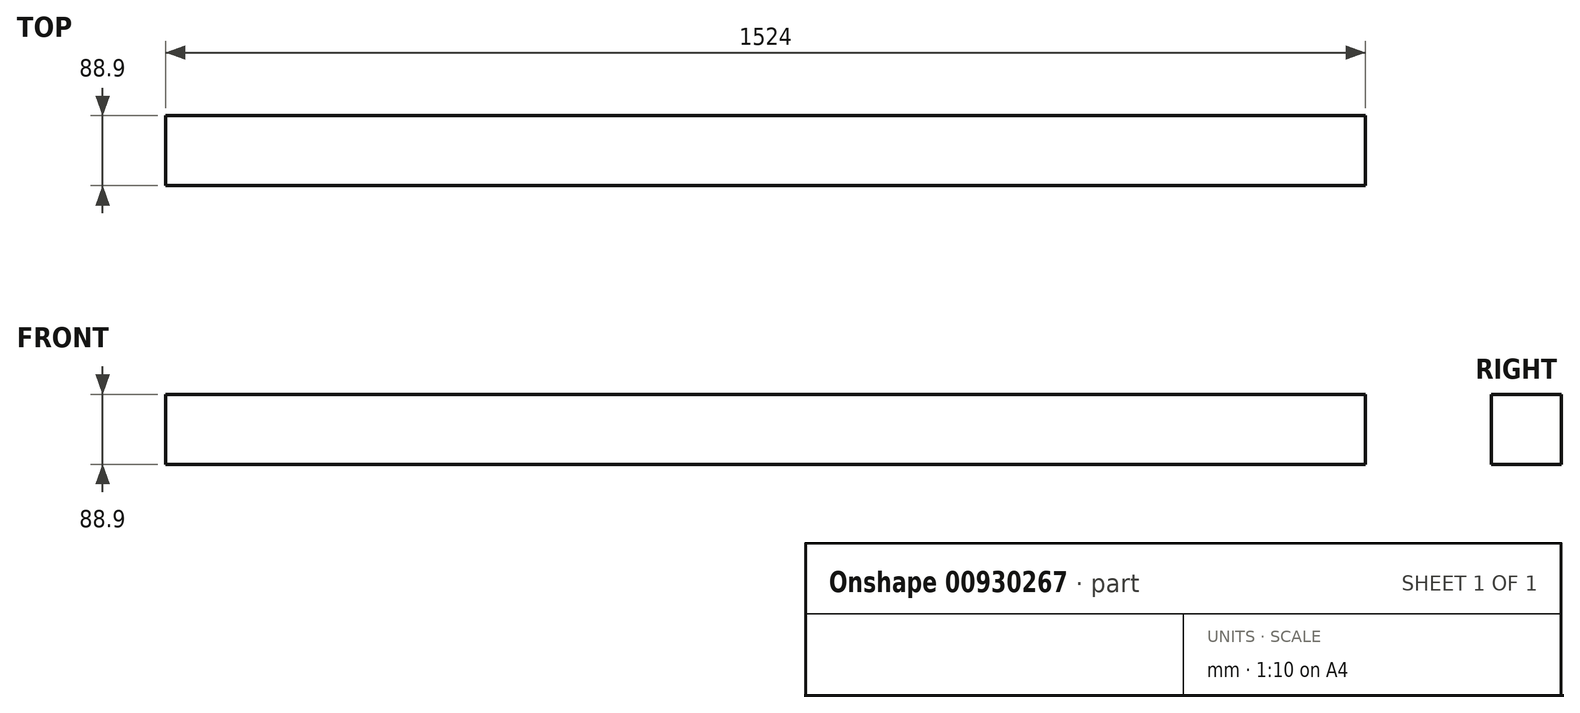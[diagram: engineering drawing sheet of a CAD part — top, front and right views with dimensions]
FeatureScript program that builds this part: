
annotation { "Feature Type Name" : "Feature", "Feature Type Description" : "" }
export const myFeature = defineFeature(function(context is Context, id is Id, definition is map)
    precondition{}
    {
        {
            var Q0;
            Q0=qCreatedBy(makeId("Right.planeOp"),FACE);
            var sketch = newSketch(context, id + "F0", { "sketchPlane" : qUnion([Q0])});
            skLineSegment(sketch, "E0.bottom", {"start": v(44.45, -44.45) * mm, "end": v(-44.45, -44.45) * mm});
            skLineSegment(sketch, "E0.top", {"start": v(44.45, 44.45) * mm, "end": v(-44.45, 44.45) * mm});
            skLineSegment(sketch, "E0.left", {"start": v(44.45, -44.45) * mm, "end": v(44.45, 44.45) * mm});
            skLineSegment(sketch, "E0.right", {"start": v(-44.45, -44.45) * mm, "end": v(-44.45, 44.45) * mm});
            skPoint(sketch, "E0.middle", {"position": v(0, 0) * mm});
            skSolve(sketch);
        }
        {
            var Q0;
            Q0=qSketchRegion(id+"F0",true);
            extrude(context, id + "F1", {"entities" : qUnion([Q0]), "endBound" : BoundingType.SYMMETRIC, "depth" : 1524 * mm});
        }
    });
